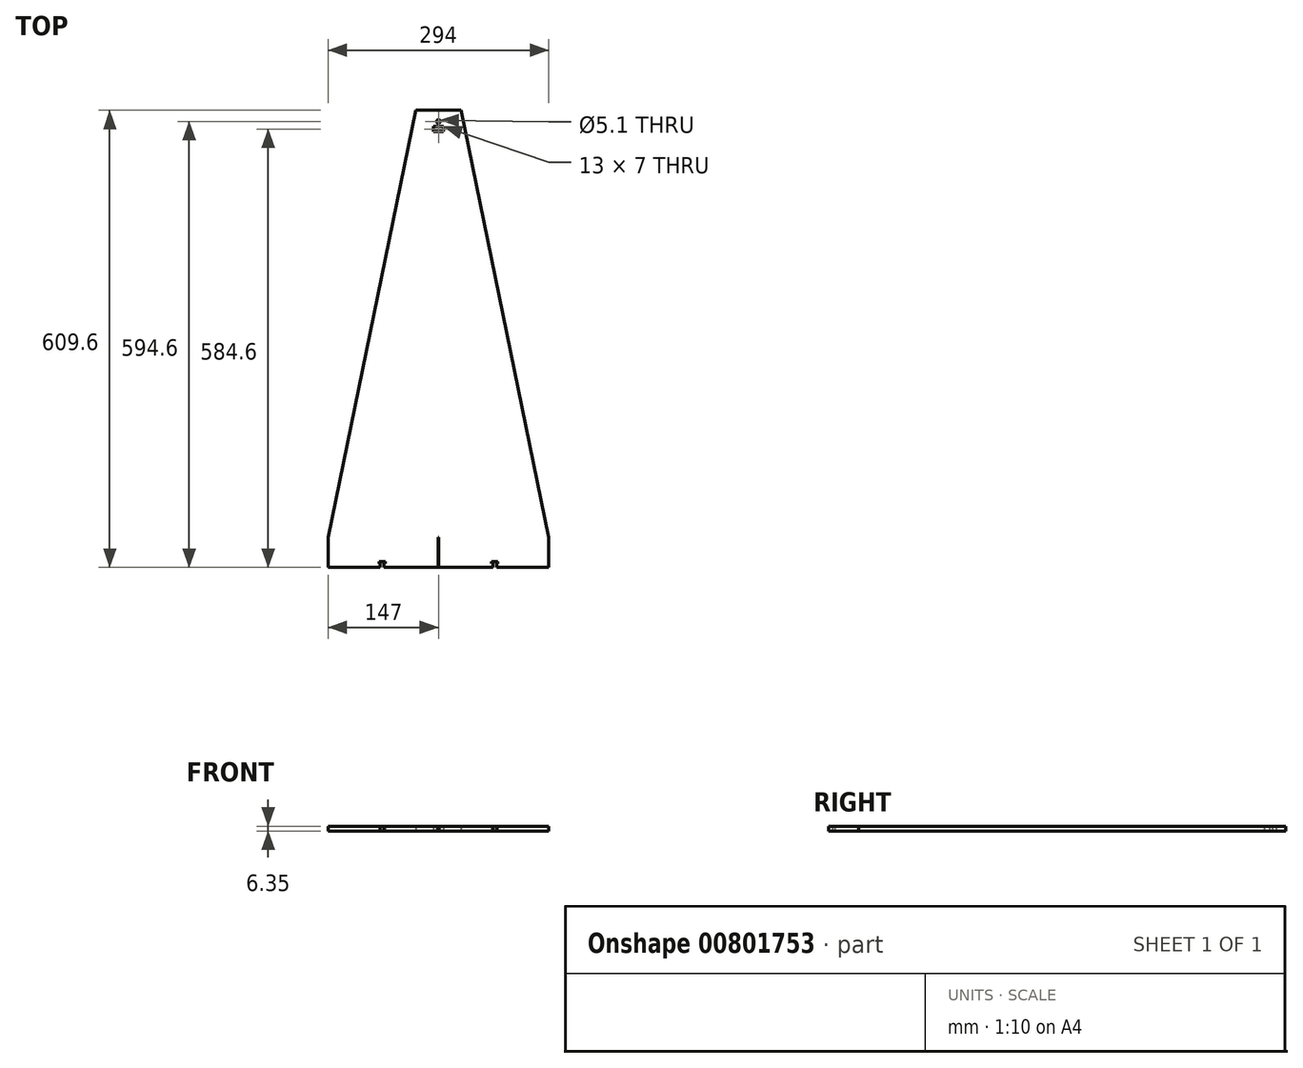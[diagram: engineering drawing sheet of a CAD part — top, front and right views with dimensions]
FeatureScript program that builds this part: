
annotation { "Feature Type Name" : "Feature", "Feature Type Description" : "" }
export const myFeature = defineFeature(function(context is Context, id is Id, definition is map)
    precondition{}
    {
        {
            var Q0;
            Q0=qCreatedBy(makeId("Top.planeOp"),FACE);
            var sketch = newSketch(context, id + "F0", { "sketchPlane" : qUnion([Q0])});
            skLineSegment(sketch, "E0.bottom", {"start": v(152.4, 304.8) * mm, "end": v(-152.4, 304.8) * mm, "construction": true});
            skLineSegment(sketch, "E0.top", {"start": v(152.4, -304.8) * mm, "end": v(-152.4, -304.8) * mm, "construction": true});
            skLineSegment(sketch, "E0.left", {"start": v(152.4, 304.8) * mm, "end": v(152.4, -304.8) * mm, "construction": true});
            skLineSegment(sketch, "E0.right", {"start": v(-152.4, 304.8) * mm, "end": v(-152.4, -304.8) * mm, "construction": true});
            skPoint(sketch, "E0.middle", {"position": v(0, 0) * mm});
            skLineSegment(sketch, "E1", {"start": v(-152.4, -264.8) * mm, "end": v(152.4, -264.8) * mm});
            skLineSegment(sketch, "E2", {"start": v(-147.4, -264.8) * mm, "end": v(-147.4, -304.8) * mm});
            skLineSegment(sketch, "E3", {"start": v(146.6, -264.8) * mm, "end": v(146.6, -304.8) * mm});
            skLineSegment(sketch, "E4", {"start": v(-147.4, -304.8) * mm, "end": v(146.6, -304.8) * mm});
            skLineSegment(sketch, "E5", {"start": v(-0.4, -304.8) * mm, "end": v(-0.4, 304.8) * mm, "construction": true});
            skLineSegment(sketch, "E6", {"start": v(-147.4, -264.8) * mm, "end": v(-30.4, 304.8) * mm});
            skLineSegment(sketch, "E7", {"start": v(-30.4, 304.8) * mm, "end": v(29.6, 304.8) * mm});
            skLineSegment(sketch, "E8", {"start": v(29.6, 304.8) * mm, "end": v(146.6, -264.8) * mm});
            skCircle(sketch, "E9", {"center": v(-0.4, 289.8) * mm, "radius": 2.55 * mm});
            skLineSegment(sketch, "E10.bottom", {"start": v(6.1, 276.3) * mm, "end": v(-6.9, 276.3) * mm});
            skLineSegment(sketch, "E10.top", {"start": v(6.1, 283.3) * mm, "end": v(-6.9, 283.3) * mm});
            skLineSegment(sketch, "E10.left", {"start": v(6.1, 276.3) * mm, "end": v(6.1, 283.3) * mm});
            skLineSegment(sketch, "E10.right", {"start": v(-6.9, 276.3) * mm, "end": v(-6.9, 283.3) * mm});
            skPoint(sketch, "E10.middle", {"position": v(-0.4, 279.8) * mm});
            skLineSegment(sketch, "E11.bottom", {"start": v(-0.9, -264.8) * mm, "end": v(0.1, -264.8) * mm});
            skLineSegment(sketch, "E11.top", {"start": v(-0.9, -304.8) * mm, "end": v(0.1, -304.8) * mm});
            skLineSegment(sketch, "E11.left", {"start": v(-0.9, -264.8) * mm, "end": v(-0.9, -304.8) * mm});
            skLineSegment(sketch, "E11.right", {"start": v(0.1, -264.8) * mm, "end": v(0.1, -304.8) * mm});
            skLineSegment(sketch, "E12.bottom", {"start": v(-77.95, -304.8) * mm, "end": v(-72.85, -304.8) * mm});
            skLineSegment(sketch, "E12.top", {"start": v(-77.95, -299.8) * mm, "end": v(-72.85, -299.8) * mm});
            skLineSegment(sketch, "E12.left", {"start": v(-77.95, -304.8) * mm, "end": v(-77.95, -299.8) * mm});
            skLineSegment(sketch, "E12.right", {"start": v(-72.85, -304.8) * mm, "end": v(-72.85, -299.8) * mm});
            skLineSegment(sketch, "E13.bottom", {"start": v(-71.35, -299.8) * mm, "end": v(-79.45, -299.8) * mm});
            skLineSegment(sketch, "E13.top", {"start": v(-71.35, -296.8) * mm, "end": v(-79.45, -296.8) * mm});
            skLineSegment(sketch, "E13.left", {"start": v(-71.35, -299.8) * mm, "end": v(-71.35, -296.8) * mm});
            skLineSegment(sketch, "E13.right", {"start": v(-79.45, -299.8) * mm, "end": v(-79.45, -296.8) * mm});
            skLineSegment(sketch, "E14", {"start": v(-75.4, -299.8) * mm, "end": v(-75.4, -304.8) * mm, "construction": true});
            skLineSegment(sketch, "E15.MirrorCS", {"start": v(-79.45, -299.8) * mm, "end": v(-71.35, -299.8) * mm});
            skLineSegment(sketch, "E16.MirrorCS", {"start": v(-72.85, -304.8) * mm, "end": v(-77.95, -304.8) * mm});
            skLineSegment(sketch, "E17.MirrorCS", {"start": v(-72.85, -299.8) * mm, "end": v(-77.95, -299.8) * mm});
            skLineSegment(sketch, "E18.MirrorCS", {"start": v(-79.45, -296.8) * mm, "end": v(-71.35, -296.8) * mm});
            skLineSegment(sketch, "E19.MirrorCS", {"start": v(-150.4, -304.8) * mm, "end": v(-150.4, 304.8) * mm, "construction": true});
            skLineSegment(sketch, "E20.MirrorCS", {"start": v(77.15, -304.8) * mm, "end": v(77.15, -299.8) * mm});
            skLineSegment(sketch, "E21.MirrorCS", {"start": v(78.65, -299.8) * mm, "end": v(78.65, -296.8) * mm});
            skLineSegment(sketch, "E22.MirrorCS", {"start": v(70.55, -296.8) * mm, "end": v(78.65, -296.8) * mm});
            skLineSegment(sketch, "E23.MirrorCS", {"start": v(70.55, -299.8) * mm, "end": v(70.55, -296.8) * mm});
            skLineSegment(sketch, "E24.MirrorCS", {"start": v(72.05, -304.8) * mm, "end": v(72.05, -299.8) * mm});
            skLineSegment(sketch, "E25.MirrorCS", {"start": v(70.55, -299.8) * mm, "end": v(78.65, -299.8) * mm});
            skSolve(sketch);
        }
        {
            var Q0;
            {var subQ1=sQuery(id+"F0.wireOp",EDGE,"E6");Q0=makeQuery(id+"F0.imprint","IMPRINT",FACE,{"disambiguationData":[TD([[makeQuery(id+"F0.imprint","IMPRINT",EDGE,{"derivedFrom":subQ1}),-1.0]])]});}
            var Q1;
            {var subQ4=sQuery(id+"F0.wireOp",EDGE,"E2");Q1=makeQuery(id+"F0.imprint","IMPRINT",FACE,{"disambiguationData":[TD([[makeQuery(id+"F0.imprint","IMPRINT",EDGE,{"derivedFrom":subQ4}),1.0]])]});}
            var Q2;
            {var subQ3=sQuery(id+"F0.wireOp",EDGE,"E3");Q2=makeQuery(id+"F0.imprint","IMPRINT",FACE,{"disambiguationData":[TD([[makeQuery(id+"F0.imprint","IMPRINT",EDGE,{"derivedFrom":subQ3}),-1.0]])]});}
            extrude(context, id + "F1", {"entities" : qUnion([Q0, Q1, Q2]), "depth" : 6.35 * mm, "offsetDistance" : 25 * mm});
        }
    });
